# Revit family: 111
name_source: partatom
category: Plumbing Fixtures
revit_build: Autodesk Revit 2018 (Build: 20190510_1515(x64)
units: mm (PartAtom-declared; Revit-internal decimal feet)

## family parameters
Cut with Voids When Loaded = No
Host = Face
OmniClass Number = 23.31.25.29.11
OmniClass Title = Hand Soap Holders
Part Type = Normal
Room Calculation Point = No
Round Connector Dimension = Use Diameter
Shared = No

## types (14) — shared parameters
Brand url = http://www.gessi.it
CW Connection = Yes
Ceramic - Black = Gessi - Ceramic - Black
Default Elevation = 1219 mm
Description = Black wall-mounted soap holder
Design country = Italy
Edition number = 1
HW Connection = Yes
IFC Classification = Furnishing Element
Installation instructions = https://www.gessi.com
Manufacturer = Gessi
Manufacturer country = Italy
Manufacturer name = Gessi
Model = 65402
OmniClass Code = 23-31 25 29 11
OmniClass Description = Hand Soap Holders
Product Guid = e10e6191-d0eb-409c-af63-f69cde92da4a
Product SKU = 65402
Product certification = https://www.gessi.com
Product data url = https://bimobject.com
Product family = VENTI20
Product group = VENTI20 ACCESSORI
Product name = 20VENTI - Black wall-mounted soap holder - 65402
Product url = https://www.gessi.com
QR code = http://bimobject.com
URL = http://www.gessi.it
Uniclass 2015 Code = Pr_40_20_76_82
Uniclass 2015 Name = Soap dishes
Vent Connection = Yes
Waste Connection = Yes
zero-valued in all types: CWFU, HWFU, WFU

## per-type parameters (varying)
| type | Faucet Material | Faucet Material - Texture - Vertical |
| Aged Bronze | Gessi - Metal - Aged Bronze | Gessi - Textured - Aged Bronze Grooves - Vertical |
| Antique Brass | Gessi - Metal - Antique Brass | Gessi - Textured - Antique Brass Grooves - Vertical |
| Black Metal | Gessi - Metal - Black Metal | Gessi - Textured - Black Metal Grooves - Vertical |
| Black Metal Brushed | Gessi - Metal - Black Metal Brushed | Gessi - Textured - Brass Brushed Grooves - Vertical |
| Brass | Gessi - Metal - Brass | Gessi - Textured - Brass Grooves - Vertical |
| Brass Brushed | Gessi - Metal - Brass Brushed | Gessi - Textured - Brass Brushed Grooves - Vertical |
| Chrome | Gessi - Metal - Chrome | Gessi - Textured - Chrome Grooves Vertical |
| Copper | Gessi - Metal - Copper | Gessi - Textured - Copper Grooves - Vertical |
| Copper Brushed | Gessi - Metal - Copper Brushed | Gessi - Textured - Copper Brushed Grooves Vertical |
| Finox | Gessi - Metal - Finox | Gessi - Textured - Finox Grooves Vertical |
| Matte Black | Gessi - Metal - Matte Black | Gessi - Textured - Matte Black Grooves Vertical |
| Nickel | Gessi - Metal - Nickel | Gessi - Textured - Nickel Grooves Vertical |
| Warm Bronze | Gessi - Metal - Warm Bronze | Gessi - Textured - Warm Bronze Grooves Vertical |
| Warm Bronze Brushed | Gessi - Metal - Warm Bronze Brushed | Gessi - Textured - Warm Bronze Brushed Grooves Vertical |

## geometry (parser evidence)
native form markers: Sweep x3
no freeform markers — native parametric forms only
